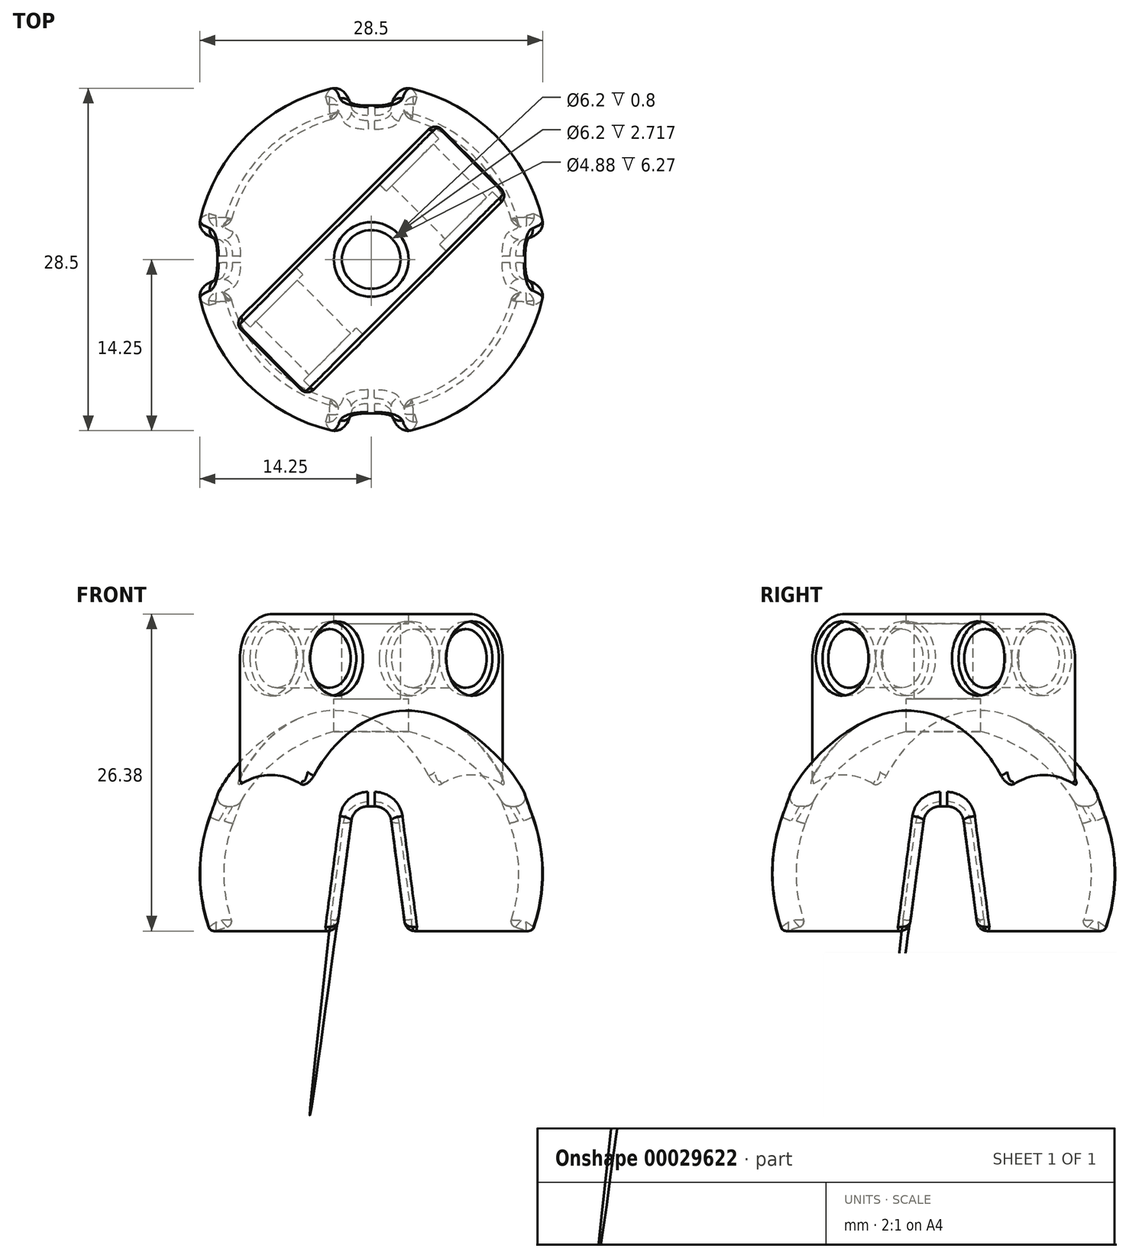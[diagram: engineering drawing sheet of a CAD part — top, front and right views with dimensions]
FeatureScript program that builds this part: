
annotation { "Feature Type Name" : "Feature", "Feature Type Description" : "" }
export const myFeature = defineFeature(function(context is Context, id is Id, definition is map)
    precondition{}
    {
        {
            var Q0;
            Q0=qCreatedBy(makeId("Front.planeOp"),FACE);
            var sketch = newSketch(context, id + "F0", { "sketchPlane" : qUnion([Q0])});
            skArc(sketch, "E0", {"start": v(12.12, -3.43) * mm, "mid": v(10.05, 7.6) * mm, "end": v(0, 12.6) * mm});
            skArc(sketch, "E1", {"start": v(14.04, -4.02) * mm, "mid": v(11.66, 8.79) * mm, "end": v(0, 14.6) * mm});
            skLineSegment(sketch, "E2", {"start": v(12.45, -4.05) * mm, "end": v(13.4, -4.35) * mm});
            skLineSegment(sketch, "E3", {"start": v(0, 0) * mm, "end": v(0, 14.6) * mm, "construction": true});
            skLineSegment(sketch, "E4", {"start": v(0, 14.6) * mm, "end": v(0, 12.6) * mm});
            skArc(sketch, "E5.filletArc", {"start": v(12.12, -3.43) * mm, "mid": v(12.16, -3.8) * mm, "end": v(12.45, -4.05) * mm});
            skPoint(sketch, "E6.visualSharp", {"position": v(13.89, -4.51) * mm});
            skArc(sketch, "E6.filletArc", {"start": v(13.4, -4.35) * mm, "mid": v(13.8, -4.32) * mm, "end": v(14.04, -4.02) * mm});
            skLineSegment(sketch, "E7", {"start": v(12.1, -3.57) * mm, "end": v(12.1, -6.08) * mm, "construction": true});
            skLineSegment(sketch, "E8", {"start": v(12.1, -3.57) * mm, "end": v(11.4, -3.57) * mm, "construction": true});
            skSolve(sketch);
        }
        {
            var Q0;
            Q0=makeQuery(id+"F0.imprint","IMPRINT",FACE,{"disambiguationData":[TD([[makeQuery(id+"F0.imprint","IMPRINT",EDGE,{"derivedFrom":sQuery(id+"F0.wireOp",EDGE,"E0")}),-1.0]])]});
            var Q1;
            Q1=sQuery(id+"F0.wireOp",EDGE,"E3");
            revolve(context, id + "F1", {"entities" : qUnion([Q0]), "axis" : qUnion([Q1]), "revolveType" : RevolveType.FULL});
        }
        {
            var Q0;
            Q0=qCreatedBy(makeId("Top.planeOp"),FACE);
            var sketch = newSketch(context, id + "F2", { "sketchPlane" : qUnion([Q0])});
            skLineSegment(sketch, "E9", {"start": v(0, 0) * mm, "end": v(-78.4, 78.4) * mm, "construction": true});
            skLineSegment(sketch, "E10", {"start": v(0, 0) * mm, "end": v(-78.9, 0) * mm, "construction": true});
            skSolve(sketch);
        }
        {
            var Q0;
            Q0=sQuery(id+"F2.wireOp",EDGE,"E9");
            var Q1;
            Q1=sQuery(id+"F2.wireOp",VERTEX,"E10.start");
            cPlane(context, id + "F3", {"entities" : qUnion([Q0, Q1]), "cplaneType" : CPlaneType.LINE_POINT, "offset" : 150 * mm, "width" : 150 * mm, "height" : 150 * mm});
        }
        {
            var Q0;
            Q0=qCreatedBy(id+"F3.planeOp",FACE);
            var sketch = newSketch(context, id + "F4", { "sketchPlane" : qUnion([Q0])});
            skArc(sketch, "E11", {"start": v(11.7, 7.69) * mm, "mid": v(0, 14) * mm, "end": v(-11.7, 7.69) * mm});
            skLineSegment(sketch, "E12.rect.bottom", {"start": v(-8, 22) * mm, "end": v(8, 22) * mm});
            skLineSegment(sketch, "E12.rect.left", {"start": v(-11.7, 18.3) * mm, "end": v(-11.7, 7.69) * mm});
            skLineSegment(sketch, "E12.rect.right", {"start": v(11.7, 18.3) * mm, "end": v(11.7, 7.69) * mm});
            skLineSegment(sketch, "E13", {"start": v(0, 0) * mm, "end": v(0, 21.87) * mm, "construction": true});
            skCircle(sketch, "E14", {"center": v(8, 18.3) * mm, "radius": 3.1 * mm});
            skCircle(sketch, "E15.MirrorC", {"center": v(-8, 18.3) * mm, "radius": 3.1 * mm});
            skPoint(sketch, "E16.visualSharp", {"position": v(11.7, 22) * mm});
            skArc(sketch, "E16.filletArc", {"start": v(11.7, 18.3) * mm, "mid": v(10.62, 20.92) * mm, "end": v(8, 22) * mm});
            skPoint(sketch, "E17.visualSharp", {"position": v(-11.7, 22) * mm});
            skArc(sketch, "E17.filletArc", {"start": v(-8, 22) * mm, "mid": v(-10.62, 20.92) * mm, "end": v(-11.7, 18.3) * mm});
            skSolve(sketch);
        }
        {
            var Q0;
            Q0=qSketchRegion(id+"F4",true);
            extrude(context, id + "F5", {"entities" : qUnion([Q0]), "operationType" : NewBodyOperationType.ADD, "endBound" : BoundingType.SYMMETRIC, "depth" : 7.85 * mm});
        }
        {
            var Q0;
            Q0=qCreatedBy(id+"F3.planeOp",FACE);
            var sketch = newSketch(context, id + "F6", { "sketchPlane" : qUnion([Q0])});
            skCircle(sketch, "E18", {"center": v(8, 18.3) * mm, "radius": 3.41 * mm});
            skCircle(sketch, "E19", {"center": v(8, 18.3) * mm, "radius": 2.44 * mm});
            skCircle(sketch, "E20", {"center": v(-8, 18.3) * mm, "radius": 2.44 * mm});
            skCircle(sketch, "E21", {"center": v(-8, 18.3) * mm, "radius": 3.58 * mm});
            skSolve(sketch);
        }
        {
            var Q0;
            Q0=qSketchRegion(id+"F6",true);
            extrude(context, id + "F7", {"entities" : qUnion([Q0]), "operationType" : NewBodyOperationType.ADD, "endBound" : BoundingType.SYMMETRIC, "depth" : 6.27 * mm});
        }
        {
            var Q0;
            Q0=makeQuery(id+"F5.opExtrude","SWEPT_FACE",FACE,{"disambiguationData":[OSD([sQuery(id+"F4.wireOp",EDGE,"E12.rect.bottom")])]});
            var sketch = newSketch(context, id + "F8", { "sketchPlane" : qUnion([Q0])});
            skCircle(sketch, "E22", {"center": v(0, 0) * mm, "radius": 3.1 * mm});
            skSolve(sketch);
        }
        {
            var Q0;
            Q0=qSketchRegion(id+"F8",true);
            extrude(context, id + "F9", {"entities" : qUnion([Q0]), "operationType" : NewBodyOperationType.REMOVE, "endBound" : BoundingType.THROUGH_ALL, "oppositeDirection" : true, "depth" : 25 * mm});
        }
        {
            var Q0;
            Q0=makeQuery(id+"F5.opExtrude","CAP_VERTEX",VERTEX,{"disambiguationData":[OSD([sQuery(id+"F4.wireOp",EDGE,"E12.rect.bottom"),sQuery(id+"F4.wireOp",EDGE,"E16.filletArc")])],"isStart":false});
            var Q1;
            Q1=makeQuery(id+"F5.opExtrude","CAP_VERTEX",VERTEX,{"disambiguationData":[OSD([sQuery(id+"F4.wireOp",EDGE,"E12.rect.bottom"),sQuery(id+"F4.wireOp",EDGE,"E16.filletArc")])],"isStart":true});
            var Q2;
            Q2=makeQuery(id+"F5.opExtrude","CAP_VERTEX",VERTEX,{"disambiguationData":[OSD([sQuery(id+"F4.wireOp",EDGE,"E12.rect.bottom"),sQuery(id+"F4.wireOp",EDGE,"E17.filletArc")])],"isStart":true});
            cPlane(context, id + "F10", {"entities" : qUnion([Q0, Q1, Q2]), "cplaneType" : CPlaneType.THREE_POINT, "offset" : 20 * mm, "width" : 150 * mm, "height" : 150 * mm});
        }
        {
            var Q0;
            Q0=qCreatedBy(id+"F10.planeOp",FACE);
            cPlane(context, id + "F11", {"entities" : qUnion([Q0]), "cplaneType" : CPlaneType.OFFSET, "offset" : 0.8 * mm, "width" : 150 * mm, "height" : 150 * mm});
        }
        {
            var Q0;
            Q0=qCreatedBy(id+"F11.planeOp",FACE);
            var sketch = newSketch(context, id + "F12", { "sketchPlane" : qUnion([Q0])});
            skCircle(sketch, "E23", {"center": v(0, 0) * mm, "radius": 2.44 * mm});
            skCircle(sketch, "E24", {"center": v(0, 0) * mm, "radius": 3.35 * mm});
            skSolve(sketch);
        }
        {
            var Q0;
            Q0=qSketchRegion(id+"F12",true);
            extrude(context, id + "F13", {"entities" : qUnion([Q0]), "operationType" : NewBodyOperationType.ADD, "depth" : 6.27 * mm});
        }
        {
            var Q0;
            Q0=makeQuery(id+"F5.opExtrude","CAP_EDGE",EDGE,{"disambiguationData":[OSD([sQuery(id+"F4.wireOp",EDGE,"E12.rect.right")])],"isStart":true});
            var Q1;
            Q1=makeQuery(id+"F5.opExtrude","CAP_EDGE",EDGE,{"disambiguationData":[OSD([sQuery(id+"F4.wireOp",EDGE,"E16.filletArc")])],"isStart":true});
            var Q2;
            Q2=makeQuery(id+"F5.opExtrude","CAP_EDGE",EDGE,{"disambiguationData":[OSD([sQuery(id+"F4.wireOp",EDGE,"E12.rect.bottom")])],"isStart":true});
            var Q3;
            Q3=makeQuery(id+"F5.opExtrude","CAP_EDGE",EDGE,{"disambiguationData":[OSD([sQuery(id+"F4.wireOp",EDGE,"E17.filletArc")])],"isStart":true});
            var Q4;
            Q4=makeQuery(id+"F5.opExtrude","CAP_EDGE",EDGE,{"disambiguationData":[OSD([sQuery(id+"F4.wireOp",EDGE,"E12.rect.right")])],"isStart":false});
            fillet(context, id + "F14", {"entities" : qUnion([Q0, Q1, Q2, Q3, Q4]), "radius" : 0.3 * mm, "tangentPropagation" : true, "allowEdgeOverflow" : false});
        }
        {
            var Q0;
            Q0=makeQuery(id+"F5.boolean.opBoolean","INTERSECT",EDGE,{"derivedFrom":[makeQuery(id+"F1.opRevolve","SWEPT_FACE",FACE,{"disambiguationData":[OSD([sQuery(id+"F0.wireOp",EDGE,"E1")])]}),makeQuery(id+"F5.opExtrude","SWEPT_FACE",FACE,{"disambiguationData":[OSD([sQuery(id+"F4.wireOp",EDGE,"E12.rect.left")])]})]});
            fillet(context, id + "F15", {"entities" : qUnion([Q0]), "radius" : .5 * mm, "tangentPropagation" : true, "allowEdgeOverflow" : false});
        }
        {
            var Q0;
            Q0=qCreatedBy(makeId("Right.planeOp"),FACE);
            var sketch = newSketch(context, id + "F16", { "sketchPlane" : qUnion([Q0])});
            skLineSegment(sketch, "E25", {"start": v(0, 0) * mm, "end": v(0, -14.3) * mm, "construction": true});
            skLineSegment(sketch, "E26", {"start": v(0, 0) * mm, "end": v(0, 6) * mm, "construction": true});
            skLineSegment(sketch, "E27", {"start": v(-3.32, -7.84) * mm, "end": v(-1.66, 4.78) * mm});
            skLineSegment(sketch, "E28", {"start": v(-0.27, 6) * mm, "end": v(0, 6) * mm});
            skPoint(sketch, "E29.visualSharp", {"position": v(-1.5, 6) * mm});
            skArc(sketch, "E29.filletArc", {"start": v(-0.27, 6) * mm, "mid": v(-1.2, 5.65) * mm, "end": v(-1.66, 4.78) * mm});
            skLineSegment(sketch, "E30", {"start": v(-3.32, -7.84) * mm, "end": v(0, -7.84) * mm});
            skLineSegment(sketch, "E31.MirrorCS", {"start": v(3.32, -7.84) * mm, "end": v(0, -7.84) * mm});
            skLineSegment(sketch, "E32.MirrorCS", {"start": v(3.32, -7.84) * mm, "end": v(1.66, 4.78) * mm});
            skArc(sketch, "E33.MirrorCS", {"start": v(0.27, 6) * mm, "mid": v(1.2, 5.65) * mm, "end": v(1.66, 4.78) * mm});
            skLineSegment(sketch, "E34.MirrorCS", {"start": v(0.27, 6) * mm, "end": v(0, 6) * mm});
            skLineSegment(sketch, "E35", {"start": v(0, 0) * mm, "end": v(0.27, 42.2) * mm, "construction": true});
            skSolve(sketch);
        }
        {
            var Q0;
            Q0 = qSketchRegion(id + "F16", true);
            extrude(context, id + "F17", {"entities" : qUnion([Q0]), "operationType" : NewBodyOperationType.REMOVE, "endBound" : BoundingType.SYMMETRIC, "oppositeDirection" : true, "depth" : 40 * mm});
        }
        {
            var Q0;
            Q0=qCreatedBy(makeId("Front.planeOp"),FACE);
            var sketch = newSketch(context, id + "F18", { "sketchPlane" : qUnion([Q0])});
            skLineSegment(sketch, "E36", {"start": v(0, 0) * mm, "end": v(0, -123.28) * mm, "construction": true});
            skLineSegment(sketch, "E37", {"start": v(0, 0) * mm, "end": v(0, 6) * mm, "construction": true});
            skLineSegment(sketch, "E38", {"start": v(-3.32, -7.84) * mm, "end": v(-1.66, 4.78) * mm});
            skLineSegment(sketch, "E39", {"start": v(-0.27, 6) * mm, "end": v(0, 6) * mm});
            skPoint(sketch, "E40.visualSharp", {"position": v(-1.5, 6) * mm});
            skArc(sketch, "E40.filletArc", {"start": v(-0.27, 6) * mm, "mid": v(-1.2, 5.65) * mm, "end": v(-1.66, 4.78) * mm});
            skLineSegment(sketch, "E41", {"start": v(-3.32, -7.84) * mm, "end": v(0, -7.84) * mm});
            skLineSegment(sketch, "E42.MirrorCS", {"start": v(3.32, -7.84) * mm, "end": v(0, -7.84) * mm});
            skLineSegment(sketch, "E43.MirrorCS", {"start": v(3.32, -7.84) * mm, "end": v(1.66, 4.78) * mm});
            skArc(sketch, "E44.MirrorCS", {"start": v(0.27, 6) * mm, "mid": v(1.2, 5.65) * mm, "end": v(1.66, 4.78) * mm});
            skLineSegment(sketch, "E45.MirrorCS", {"start": v(0.27, 6) * mm, "end": v(0, 6) * mm});
            skLineSegment(sketch, "E46", {"start": v(0, 0) * mm, "end": v(0.27, 42.2) * mm, "construction": true});
            skSolve(sketch);
        }
        {
            var Q0;
            Q0 = qSketchRegion(id + "F18", true);
            extrude(context, id + "F19", {"entities" : qUnion([Q0]), "operationType" : NewBodyOperationType.REMOVE, "endBound" : BoundingType.SYMMETRIC, "oppositeDirection" : true, "depth" : 40 * mm});
        }
        {
            var Q0;
            Q0=makeQuery(id+"F17.boolean.opBoolean","INTERSECT",EDGE,{"disambiguationData":[OD(0.0)],"derivedFrom":[makeQuery(id+"F1.opRevolve","SWEPT_FACE",FACE,{"disambiguationData":[OSD([sQuery(id+"F0.wireOp",EDGE,"E1")])]}),makeQuery(id+"F17.opExtrude","SWEPT_FACE",FACE,{"disambiguationData":[OSD([sQuery(id+"F16.wireOp",EDGE,"E32.MirrorCS")])]})]});
            var Q1;
            Q1=makeQuery(id+"F19.boolean.opBoolean","INTERSECT",EDGE,{"disambiguationData":[OD(0.0)],"derivedFrom":[makeQuery(id+"F1.opRevolve","SWEPT_FACE",FACE,{"disambiguationData":[OSD([sQuery(id+"F0.wireOp",EDGE,"E1")])]}),makeQuery(id+"F19.opExtrude","SWEPT_FACE",FACE,{"disambiguationData":[OSD([sQuery(id+"F18.wireOp",EDGE,"E43.MirrorCS")])]})]});
            var Q2;
            Q2=makeQuery(id+"F17.boolean.opBoolean","INTERSECT",EDGE,{"disambiguationData":[OD(1.0)],"derivedFrom":[makeQuery(id+"F1.opRevolve","SWEPT_FACE",FACE,{"disambiguationData":[OSD([sQuery(id+"F0.wireOp",EDGE,"E1")])]}),makeQuery(id+"F17.opExtrude","SWEPT_FACE",FACE,{"disambiguationData":[OSD([sQuery(id+"F16.wireOp",EDGE,"E32.MirrorCS")])]})]});
            var Q3;
            Q3=makeQuery(id+"F19.boolean.opBoolean","INTERSECT",EDGE,{"disambiguationData":[OD(1.0)],"derivedFrom":[makeQuery(id+"F1.opRevolve","SWEPT_FACE",FACE,{"disambiguationData":[OSD([sQuery(id+"F0.wireOp",EDGE,"E1")])]}),makeQuery(id+"F19.opExtrude","SWEPT_FACE",FACE,{"disambiguationData":[OSD([sQuery(id+"F18.wireOp",EDGE,"E38")])]})]});
            fillet(context, id + "F20", {"entities" : qUnion([Q0, Q1, Q2, Q3]), "radius" : .8 * mm, "tangentPropagation" : true, "allowEdgeOverflow" : false});
        }
    });
